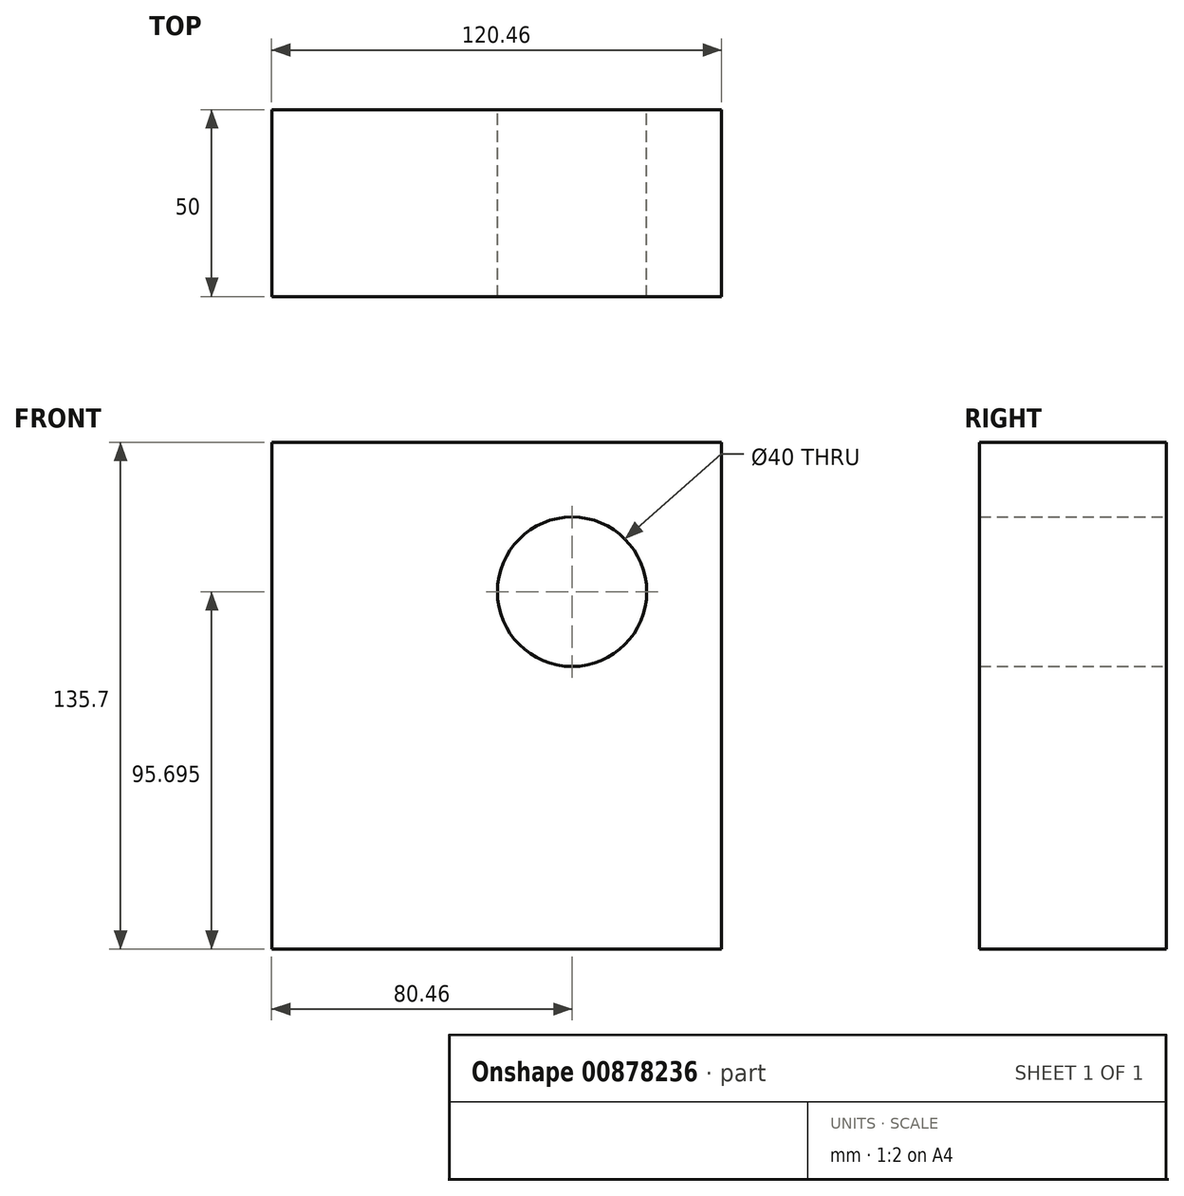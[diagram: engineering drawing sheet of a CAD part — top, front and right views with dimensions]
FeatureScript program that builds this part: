
annotation { "Feature Type Name" : "Feature", "Feature Type Description" : "" }
export const myFeature = defineFeature(function(context is Context, id is Id, definition is map)
    precondition{}
    {
        {
            var Q0;
            Q0=qCreatedBy(makeId("Front.planeOp"),FACE);
            var sketch = newSketch(context, id + "F0", { "sketchPlane" : qUnion([Q0])});
            skLineSegment(sketch, "E0.bottom", {"start": v(0, 0) * mm, "end": v(-120.46, 0) * mm});
            skLineSegment(sketch, "E0.top", {"start": v(0, 135.7) * mm, "end": v(-120.46, 135.7) * mm});
            skLineSegment(sketch, "E0.left", {"start": v(0, 0) * mm, "end": v(0, 135.7) * mm});
            skLineSegment(sketch, "E0.right", {"start": v(-120.46, 0) * mm, "end": v(-120.46, 135.7) * mm});
            skSolve(sketch);
        }
        {
            var Q0;
            Q0=makeQuery(id+"F0.imprint","IMPRINT",FACE,{"disambiguationData":[TD([[makeQuery(id+"F0.imprint","IMPRINT",EDGE,{"derivedFrom":sQuery(id+"F0.wireOp",EDGE,"E0.bottom")}),-1.0]])]});
            extrude(context, id + "F1", {"entities" : qUnion([Q0]), "depth" : 50 * mm, "offsetDistance" : 25 * mm});
        }
        {
            var Q0;
            Q0=makeQuery(id+"F1.opExtrude","CAP_FACE",FACE,{"disambiguationData":[OSD([sQuery(id+"F0.wireOp",EDGE,"E0.bottom"),sQuery(id+"F0.wireOp",EDGE,"E0.top"),sQuery(id+"F0.wireOp",EDGE,"E0.left"),sQuery(id+"F0.wireOp",EDGE,"E0.right")])],"isStart":true});
            var sketch = newSketch(context, id + "F2", { "sketchPlane" : qUnion([Q0])});
            skCircle(sketch, "E1", {"center": v(40, 95.7) * mm, "radius": 20 * mm});
            skSolve(sketch);
        }
        {
            var Q0;
            Q0=makeQuery(id+"F2.imprint","IMPRINT",FACE,{"disambiguationData":[TD([[makeQuery(id+"F2.imprint","IMPRINT",EDGE,{"derivedFrom":sQuery(id+"F2.wireOp",EDGE,"E1")}),1.0]])]});
            var Q1;
            Q1=makeQuery(id+"F1.opExtrude","CAP_FACE",FACE,{"disambiguationData":[OSD([sQuery(id+"F0.wireOp",EDGE,"E0.bottom"),sQuery(id+"F0.wireOp",EDGE,"E0.top"),sQuery(id+"F0.wireOp",EDGE,"E0.left"),sQuery(id+"F0.wireOp",EDGE,"E0.right")])],"isStart":false});
            extrude(context, id + "F3", {"entities" : qUnion([Q0]), "operationType" : NewBodyOperationType.REMOVE, "endBound" : BoundingType.UP_TO_SURFACE, "oppositeDirection" : true, "depth" : 25 * mm, "endBoundEntityFace" : qUnion([Q1]), "offsetDistance" : 25 * mm});
        }
    });
